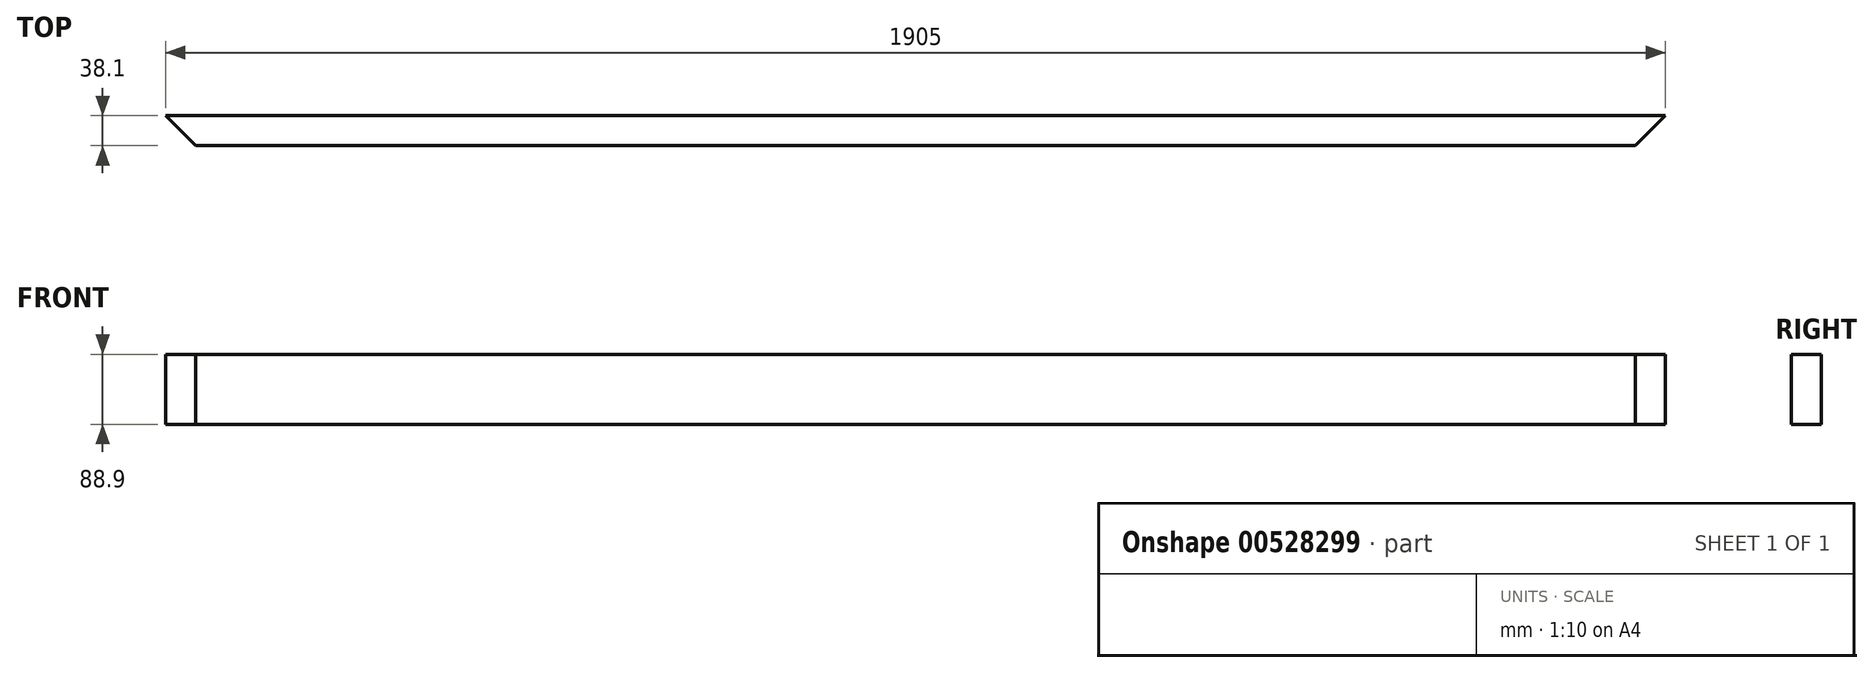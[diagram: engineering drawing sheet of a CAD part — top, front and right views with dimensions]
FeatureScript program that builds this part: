
annotation { "Feature Type Name" : "Feature", "Feature Type Description" : "" }
export const myFeature = defineFeature(function(context is Context, id is Id, definition is map)
    precondition{}
    {
        {
            var Q0;
            Q0=qCreatedBy(makeId("Top.planeOp"),FACE);
            var sketch = newSketch(context, id + "F0", { "sketchPlane" : qUnion([Q0])});
            skLineSegment(sketch, "E0.bottom", {"start": v(838.02, 124.06) * mm, "end": v(-990.78, 124.06) * mm});
            skLineSegment(sketch, "E0.top", {"start": v(876.12, 162.16) * mm, "end": v(-1028.88, 162.16) * mm});
            skPoint(sketch, "E0.middle", {"position": v(0, 0) * mm});
            skLineSegment(sketch, "E1", {"start": v(-1028.88, 162.16) * mm, "end": v(-990.78, 124.06) * mm});
            skLineSegment(sketch, "E2", {"start": v(838.02, 124.06) * mm, "end": v(876.12, 162.16) * mm});
            skSolve(sketch);
        }
        {
            var Q0;
            Q0=makeQuery(id+"F0.imprint","IMPRINT",FACE,{"disambiguationData":[TD([[makeQuery(id+"F0.imprint","IMPRINT",EDGE,{"derivedFrom":sQuery(id+"F0.wireOp",EDGE,"E0.bottom")}),-1.0]])]});
            extrude(context, id + "F1", {"entities" : qUnion([Q0]), "depth" : 88.9 * mm, "offsetDistance" : 25.4 * mm});
        }
    });
